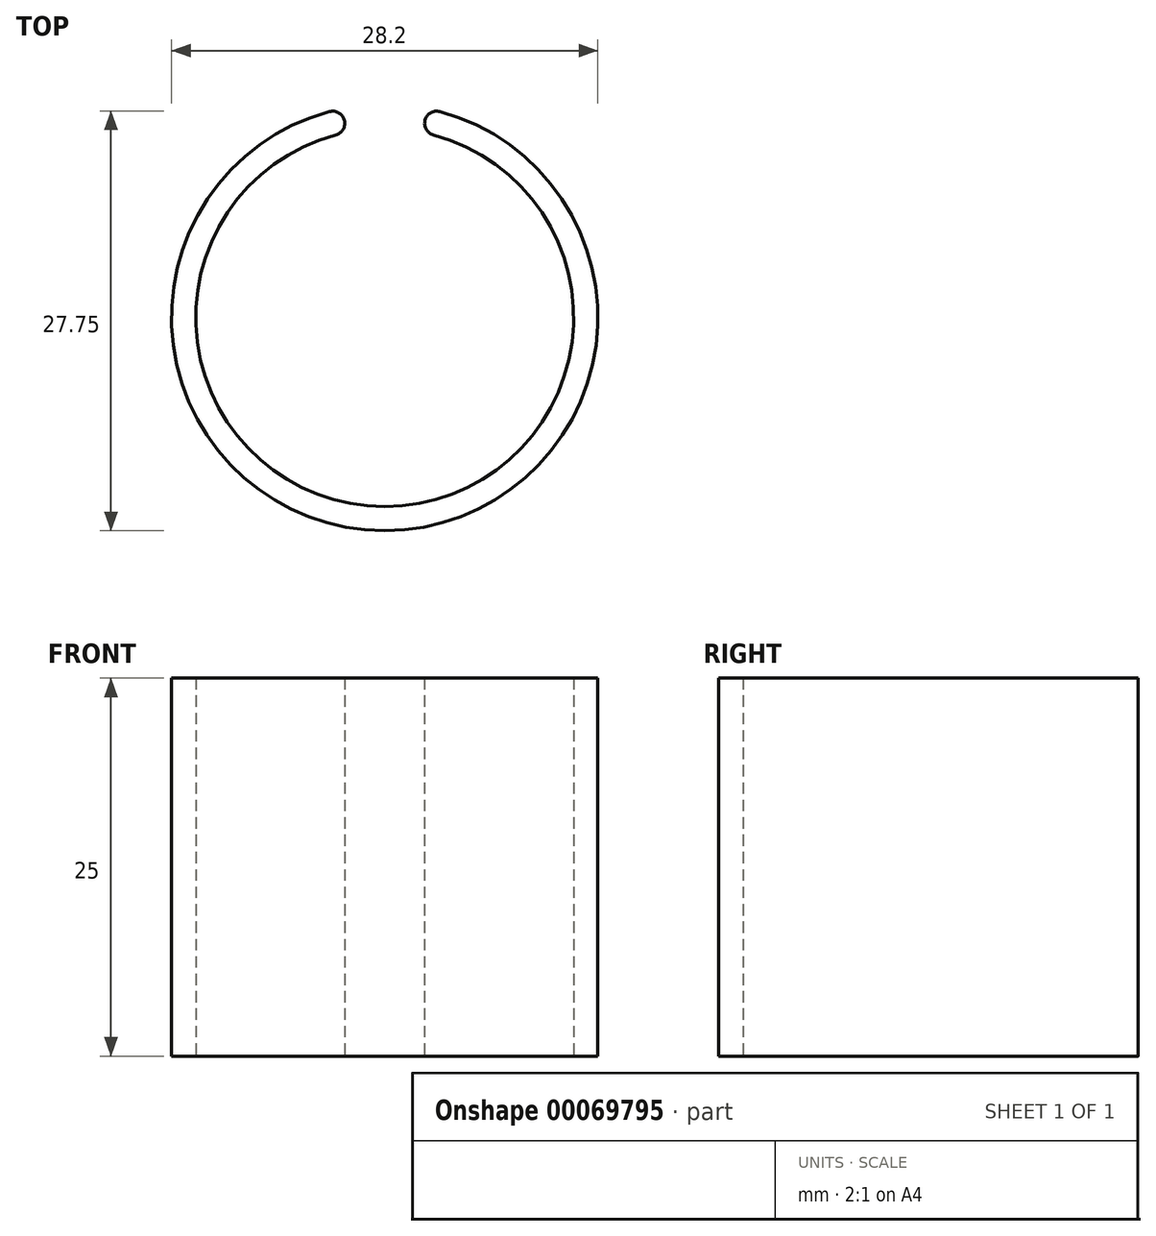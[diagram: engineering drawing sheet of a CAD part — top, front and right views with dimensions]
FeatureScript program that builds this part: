
annotation { "Feature Type Name" : "Feature", "Feature Type Description" : "" }
export const myFeature = defineFeature(function(context is Context, id is Id, definition is map)
    precondition{}
    {
        {
            var Q0;
            Q0=qCreatedBy(makeId("Top.planeOp"),FACE);
            var sketch = newSketch(context, id + "F0", { "sketchPlane" : qUnion([Q0])});
            skArc(sketch, "E0", {"start": v(-3.24, 12.07) * mm, "mid": v(0, -12.5) * mm, "end": v(3.24, 12.07) * mm});
            skArc(sketch, "E1", {"start": v(-3.65, 13.62) * mm, "mid": v(0, -14.1) * mm, "end": v(3.65, 13.62) * mm});
            skLineSegment(sketch, "E2", {"start": v(0, 0) * mm, "end": v(3.65, 13.62) * mm, "construction": true});
            skLineSegment(sketch, "E3", {"start": v(0, 0) * mm, "end": v(-3.65, 13.62) * mm, "construction": true});
            skArc(sketch, "E4", {"start": v(-3.65, 13.62) * mm, "mid": v(-2.67, 13.05) * mm, "end": v(-3.24, 12.07) * mm});
            skArc(sketch, "E5", {"start": v(3.65, 13.62) * mm, "mid": v(2.67, 13.05) * mm, "end": v(3.24, 12.07) * mm});
            skSolve(sketch);
        }
        {
            var Q0;
            Q0=makeQuery(id+"F0.imprint","IMPRINT",FACE,{"disambiguationData":[TD([[makeQuery(id+"F0.imprint","IMPRINT",EDGE,{"derivedFrom":sQuery(id+"F0.wireOp",EDGE,"E0")}),-1.0]])]});
            extrude(context, id + "F1", {"entities" : qUnion([Q0]), "depth" : 25 * mm});
        }
    });
